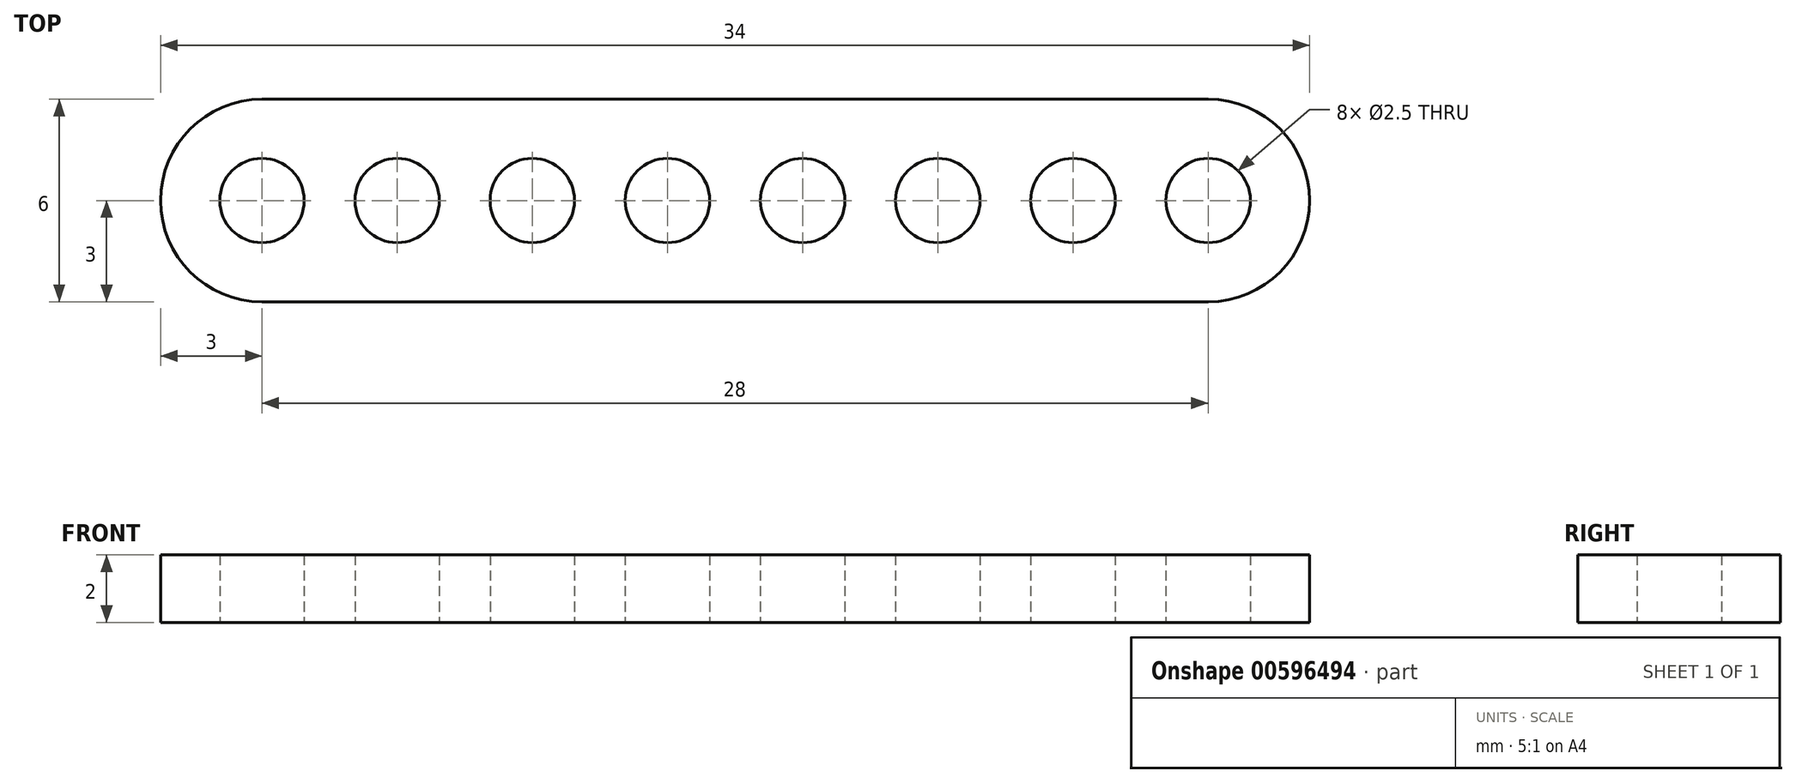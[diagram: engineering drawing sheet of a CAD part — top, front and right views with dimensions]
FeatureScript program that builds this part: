
annotation { "Feature Type Name" : "Feature", "Feature Type Description" : "" }
export const myFeature = defineFeature(function(context is Context, id is Id, definition is map)
    precondition{}
    {
        {
            var Q0;
            Q0=qCreatedBy(makeId("Top.planeOp"),FACE);
            var sketch = newSketch(context, id + "F0", { "sketchPlane" : qUnion([Q0])});
            skCircle(sketch, "E0", {"center": v(0, 0) * mm, "radius": 1.25 * mm});
            skCircle(sketch, "E1.1.0.0", {"center": v(4, 0) * mm, "radius": 1.25 * mm});
            skCircle(sketch, "E1.2.0.0", {"center": v(8, 0) * mm, "radius": 1.25 * mm});
            skCircle(sketch, "E1.3.0.0", {"center": v(12, 0) * mm, "radius": 1.25 * mm});
            skCircle(sketch, "E1.4.0.0", {"center": v(16, 0) * mm, "radius": 1.25 * mm});
            skCircle(sketch, "E1.5.0.0", {"center": v(20, 0) * mm, "radius": 1.25 * mm});
            skCircle(sketch, "E1.6.0.0", {"center": v(24, 0) * mm, "radius": 1.25 * mm});
            skCircle(sketch, "E1.7.0.0", {"center": v(28, 0) * mm, "radius": 1.25 * mm});
            skLineSegment(sketch, "E1.direction1", {"start": v(0, 0) * mm, "end": v(4, 0) * mm, "construction": true});
            skArc(sketch, "E2", {"start": v(0, -3) * mm, "mid": v(-3, 0) * mm, "end": v(0, 3) * mm});
            skArc(sketch, "E3", {"start": v(28, 3) * mm, "mid": v(31, 0) * mm, "end": v(28, -3) * mm});
            skLineSegment(sketch, "E4", {"start": v(0, 3) * mm, "end": v(28, 3) * mm});
            skLineSegment(sketch, "E5", {"start": v(28, -3) * mm, "end": v(0, -3) * mm});
            skSolve(sketch);
        }
        {
            var Q0;
            Q0=makeQuery(id+"F0.imprint","IMPRINT",FACE,{"disambiguationData":[TD([[makeQuery(id+"F0.imprint","IMPRINT",EDGE,{"derivedFrom":sQuery(id+"F0.wireOp",EDGE,"E0")}),-1.0]])]});
            extrude(context, id + "F1", {"entities" : qUnion([Q0]), "depth" : 2 * mm, "offsetDistance" : 25 * mm});
        }
    });
